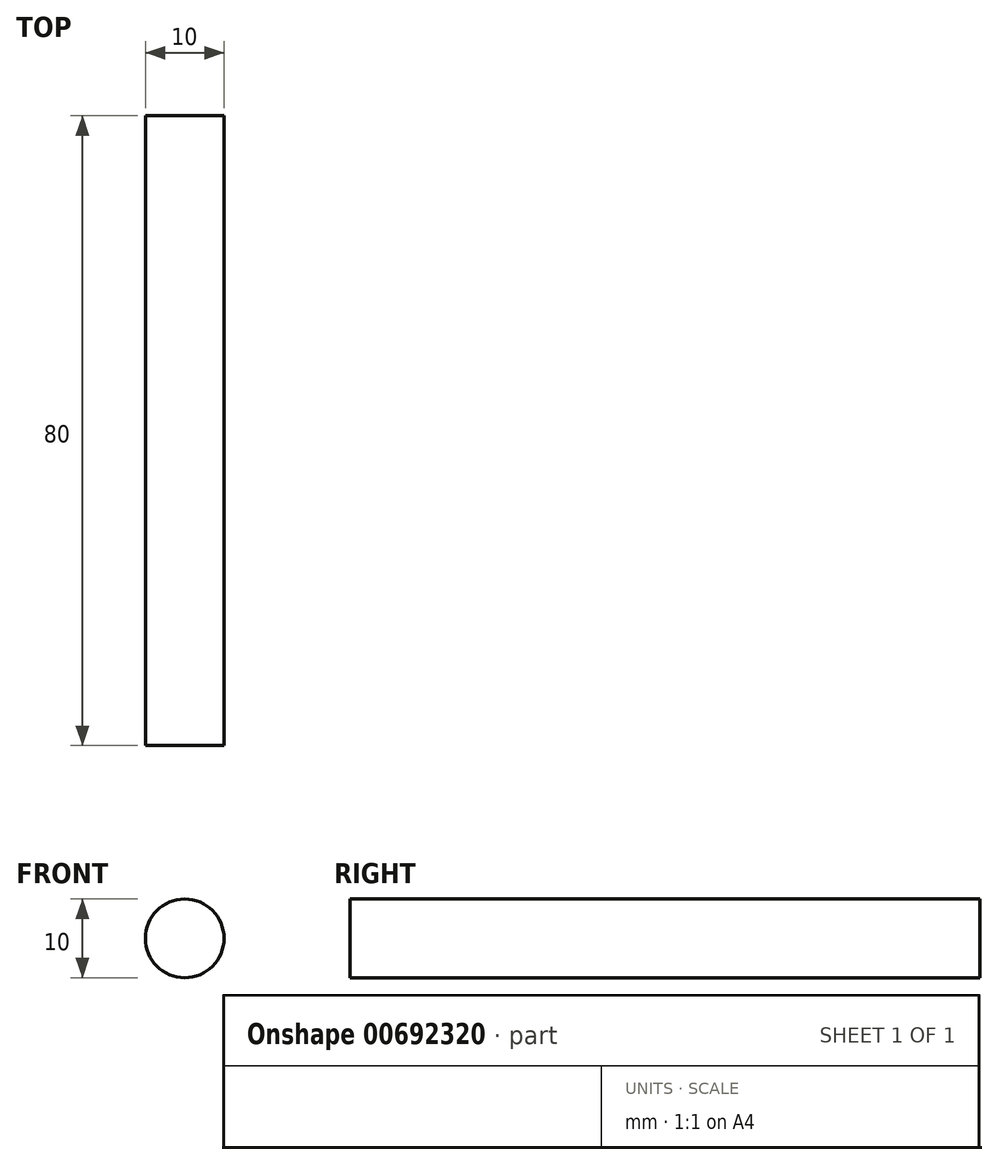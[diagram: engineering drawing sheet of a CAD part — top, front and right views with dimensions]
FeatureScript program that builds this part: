
annotation { "Feature Type Name" : "Feature", "Feature Type Description" : "" }
export const myFeature = defineFeature(function(context is Context, id is Id, definition is map)
    precondition{}
    {
        {
            var Q0;
            Q0=qCreatedBy(makeId("Front.planeOp"),FACE);
            var sketch = newSketch(context, id + "F0", { "sketchPlane" : qUnion([Q0])});
            skCircle(sketch, "E0", {"center": v(0, 0) * mm, "radius": 5 * mm});
            skSolve(sketch);
        }
        {
            var Q0;
            Q0=makeQuery(id+"F0.imprint","IMPRINT",FACE,{"disambiguationData":[TD([[makeQuery(id+"F0.imprint","IMPRINT",EDGE,{"derivedFrom":sQuery(id+"F0.wireOp",EDGE,"E0")}),1.0]])]});
            extrude(context, id + "F1", {"entities" : qUnion([Q0]), "endBound" : BoundingType.SYMMETRIC, "depth" : 80 * mm, "offsetDistance" : 25 * mm});
        }
    });
